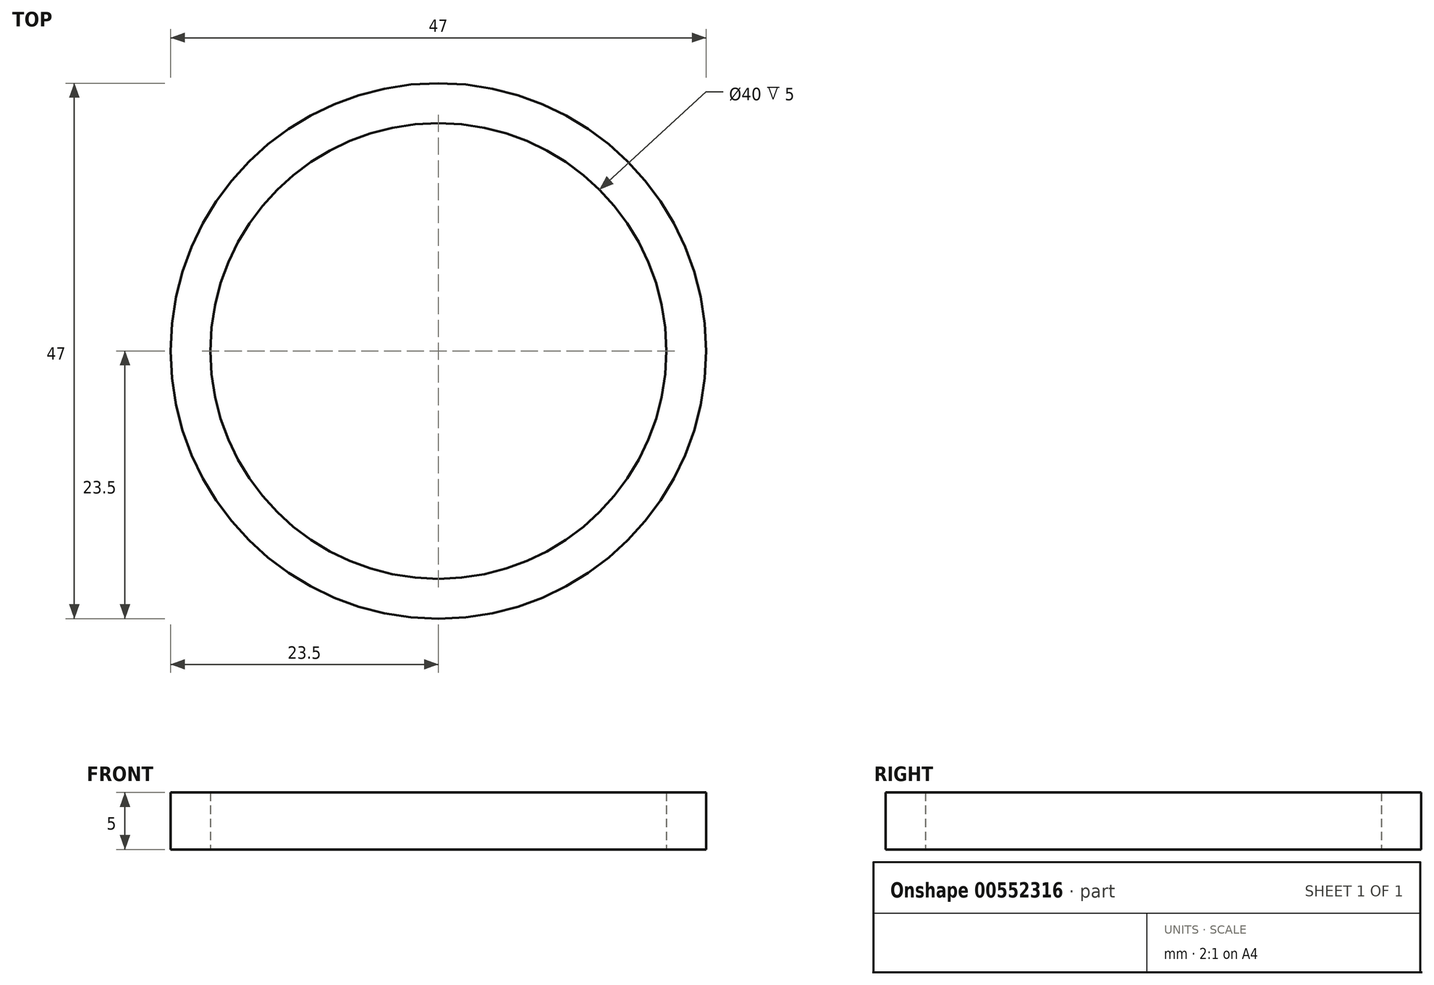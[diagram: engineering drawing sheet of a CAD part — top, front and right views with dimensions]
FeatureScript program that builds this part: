
annotation { "Feature Type Name" : "Feature", "Feature Type Description" : "" }
export const myFeature = defineFeature(function(context is Context, id is Id, definition is map)
    precondition{}
    {
        {
            var Q0;
            Q0=qCreatedBy(makeId("Top.planeOp"),FACE);
            var sketch = newSketch(context, id + "F0", { "sketchPlane" : qUnion([Q0])});
            skCircle(sketch, "E0", {"center": v(0, 0) * mm, "radius": 23.5 * mm});
            skCircle(sketch, "E1", {"center": v(0, 0) * mm, "radius": 20 * mm});
            skSolve(sketch);
        }
        {
            var Q0;
            Q0 = qSketchRegion(id + "F0", true);
            extrude(context, id + "F1", {"entities" : qUnion([Q0]), "depth" : 5 * mm, "offsetDistance" : 25 * mm});
        }
    });
